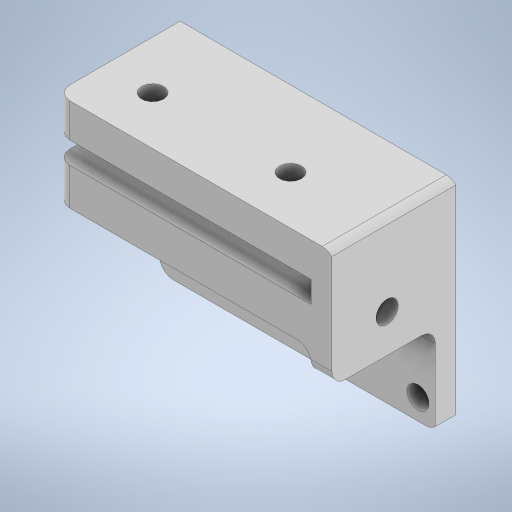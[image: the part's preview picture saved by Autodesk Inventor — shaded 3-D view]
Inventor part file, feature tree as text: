
AUTODESK INVENTOR PART (.ipt)
format: ipt  version: 2024.3 (Build 283343000, 343)  size: 358,912 bytes
history: native  units: mm
features: sketch x8, extrude x6, hole x2, fillet x2, other x1, mirror x1, projected_geometry x1
ambient origin geometry x8: Origin, YZ Plane, XZ Plane, XY Plane, X Axis, Y Axis, Z Axis, Center Point
bodies: Body1 (feature_tree)
feature tree (21):
  other  "ソリッド1"
  extrude  "押し出し1"  Depth=40.0mm
  extrude  "押し出し2"  Depth=30.0mm
  hole  "穴1"  [1 undecoded]
  extrude  "押し出し4"  Depth=3.0mm
  extrude  "押し出し5"  Depth=15.0mm TaperAngle=0.0deg
  extrude  "押し出し7"  Depth=3.0mm
  fillet  "フィレット1"  Radius=3.0mm
  fillet  "フィレット2"  Radius=15.0mm
  hole  "穴3"  [1 undecoded]
  mirror  "ミラー1"
  extrude  "押し出し9"  Depth=18.5mm
  sketch  "スケッチ1"
  sketch  "スケッチ2"
  sketch  "スケッチ5"
  sketch  "スケッチ8"
  sketch  "スケッチ9"
  projected_geometry  "投影ループ1"
  sketch  "スケッチ12"
  sketch  "スケッチ14"
  sketch  "スケッチ15"
note: 2 required parameter values undecoded (feature->parameter linkage not recoverable at this tier; creation-order binding heuristic only, values carry confidence <= 0.55)
